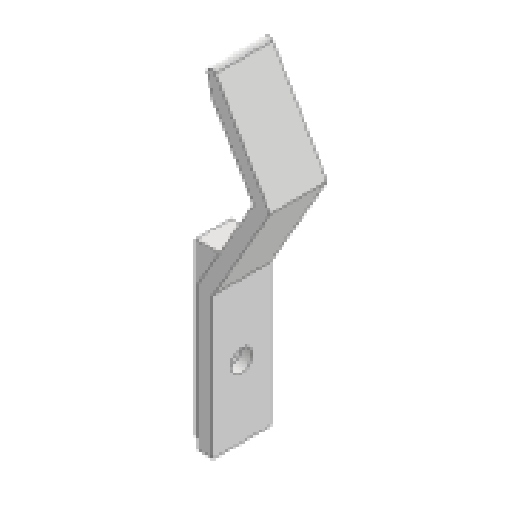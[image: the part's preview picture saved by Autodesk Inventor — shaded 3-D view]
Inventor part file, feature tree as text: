
AUTODESK INVENTOR PART (.ipt)
format: ipt  version: 2025.1 (Build 291241020, 241B)  size: 138,752 bytes
history: native  units: in
note: dims shown in document units (in); Inventor stores cm internally (conversion verified against a paired STEP export)
features: extrude x5, sketch x5, projected_geometry x2, fillet x1
ambient origin geometry x8: Origin, YZ Plane, XZ Plane, XY Plane, X Axis, Y Axis, Z Axis, Center Point
bodies: Solid1 (feature_tree)
feature tree (13):
  extrude  "Extrusion1"  Depth=0.2in
  fillet  "Fillet1"  Radius=0.8in
  extrude  "Extrusion2"  Depth=0.2in
  extrude  "Extrusion3"  TaperAngle=120.0deg  [1 undecoded]
  extrude  "Extrusion4"  Depth=1.525in
  extrude  "Extrusion5"  Depth=0.0625in
  sketch  "Sketch1"  dims[d0=2.038in d1=0.2in d4=0.8in d5=0.0in]
  sketch  "Sketch2"  dims[d6=0.2in d7=0.2in]
  sketch  "Sketch3"  dims[d8=30.0deg d10=120.0deg]
  sketch  "Sketch4"  dims[d11=2.0in d12=1.525in]
  projected_geometry  "Projected Loop1"
  sketch  "Sketch5"  dims[d13=15.0deg d14=0.0625in d15=0.49in d16=0.245in d17=2.384in d18=0.2in d19=0.0in d20=0.14in d21=0.7375in d22=0.0in d23=0.3in d24=0.158in d25=0.0in d26=1.0in d27=0.0in]
  projected_geometry  "Projected Loop2"
note: 1 required parameter value undecoded (feature->parameter linkage not recoverable at this tier; creation-order binding heuristic only, values carry confidence <= 0.55)
